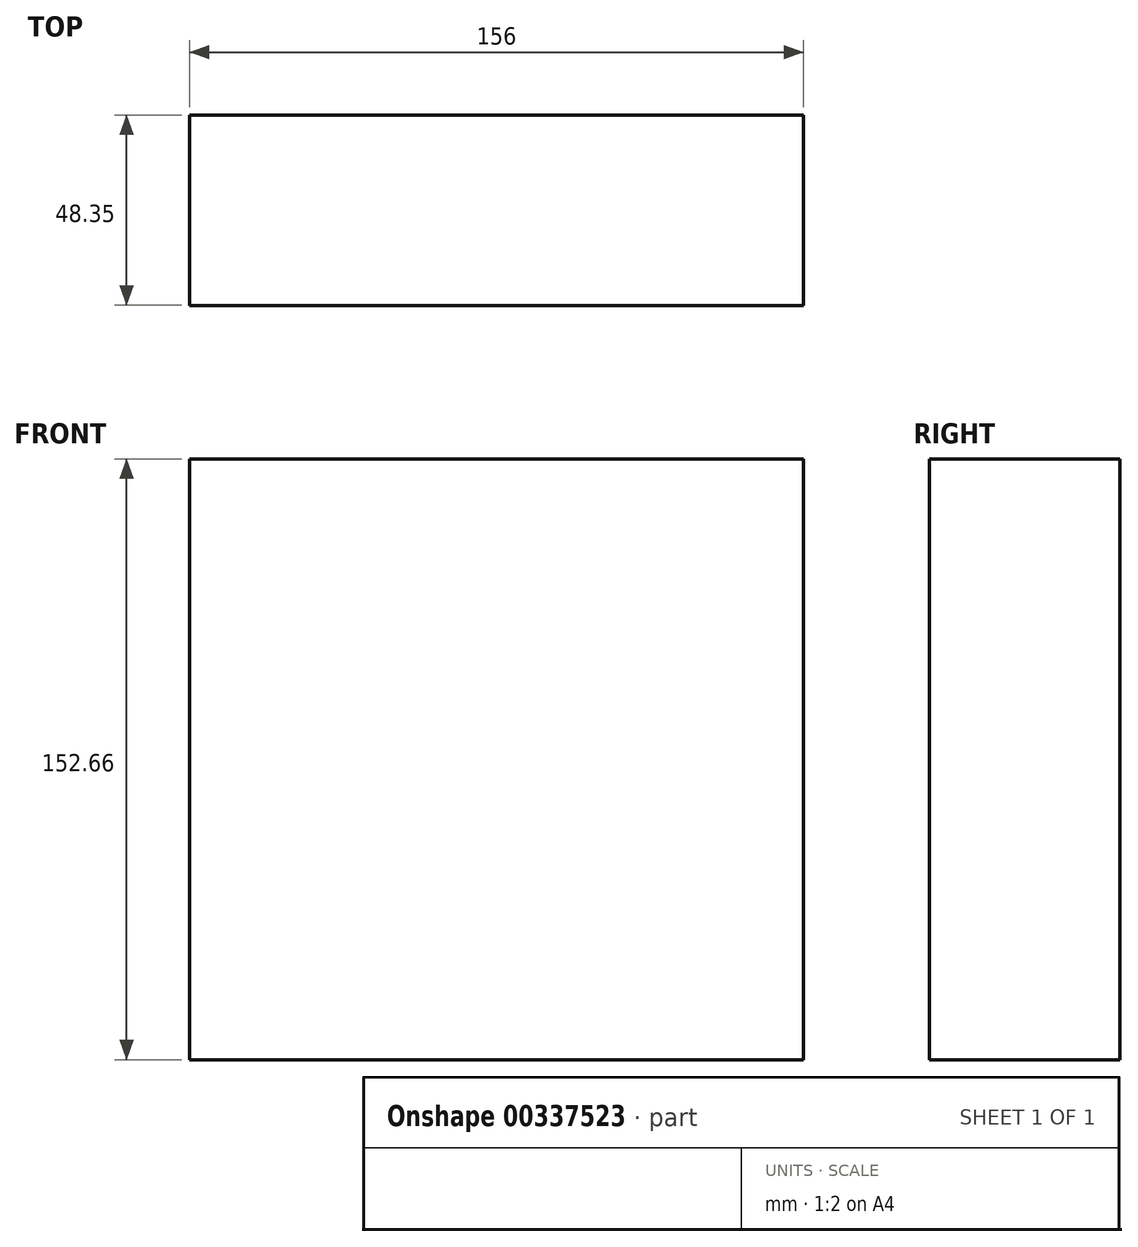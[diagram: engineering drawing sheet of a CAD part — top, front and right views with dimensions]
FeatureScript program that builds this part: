
annotation { "Feature Type Name" : "Feature", "Feature Type Description" : "" }
export const myFeature = defineFeature(function(context is Context, id is Id, definition is map)
    precondition{}
    {
        {
            var Q0;
            Q0=qCreatedBy(makeId("Front.planeOp"),FACE);
            var sketch = newSketch(context, id + "F0", { "sketchPlane" : qUnion([Q0])});
            skLineSegment(sketch, "E0.bottom", {"start": v(78, 76.33) * mm, "end": v(-78, 76.33) * mm});
            skLineSegment(sketch, "E0.top", {"start": v(78, -76.33) * mm, "end": v(-78, -76.33) * mm});
            skLineSegment(sketch, "E0.left", {"start": v(78, 76.33) * mm, "end": v(78, -76.33) * mm});
            skLineSegment(sketch, "E0.right", {"start": v(-78, 76.33) * mm, "end": v(-78, -76.33) * mm});
            skPoint(sketch, "E0.middle", {"position": v(0, 0) * mm});
            skSolve(sketch);
        }
        {
            var Q0;
            Q0=makeQuery(id+"F0.imprint","IMPRINT",FACE,{"disambiguationData":[TD([[makeQuery(id+"F0.imprint","IMPRINT",EDGE,{"derivedFrom":sQuery(id+"F0.wireOp",EDGE,"E0.bottom")}),1.0]])]});
            var sketch = newSketch(context, id + "F1", { "sketchPlane" : qUnion([Q0])});
            skSolve(sketch);
        }
        {
            var Q0;
            Q0=makeQuery(id+"F1.imprint","IMPRINT",FACE,{"disambiguationData":[TD([[makeQuery(id+"F1.imprint","IMPRINT",EDGE,{"derivedFrom":makeQuery(id+"F0.imprint","IMPRINT",EDGE,{"derivedFrom":sQuery(id+"F0.wireOp",EDGE,"E0.bottom")})}),1.0]])]});
            extrude(context, id + "F2", {"entities" : qUnion([Q0]), "depth" : 48.35 * mm});
        }
    });
